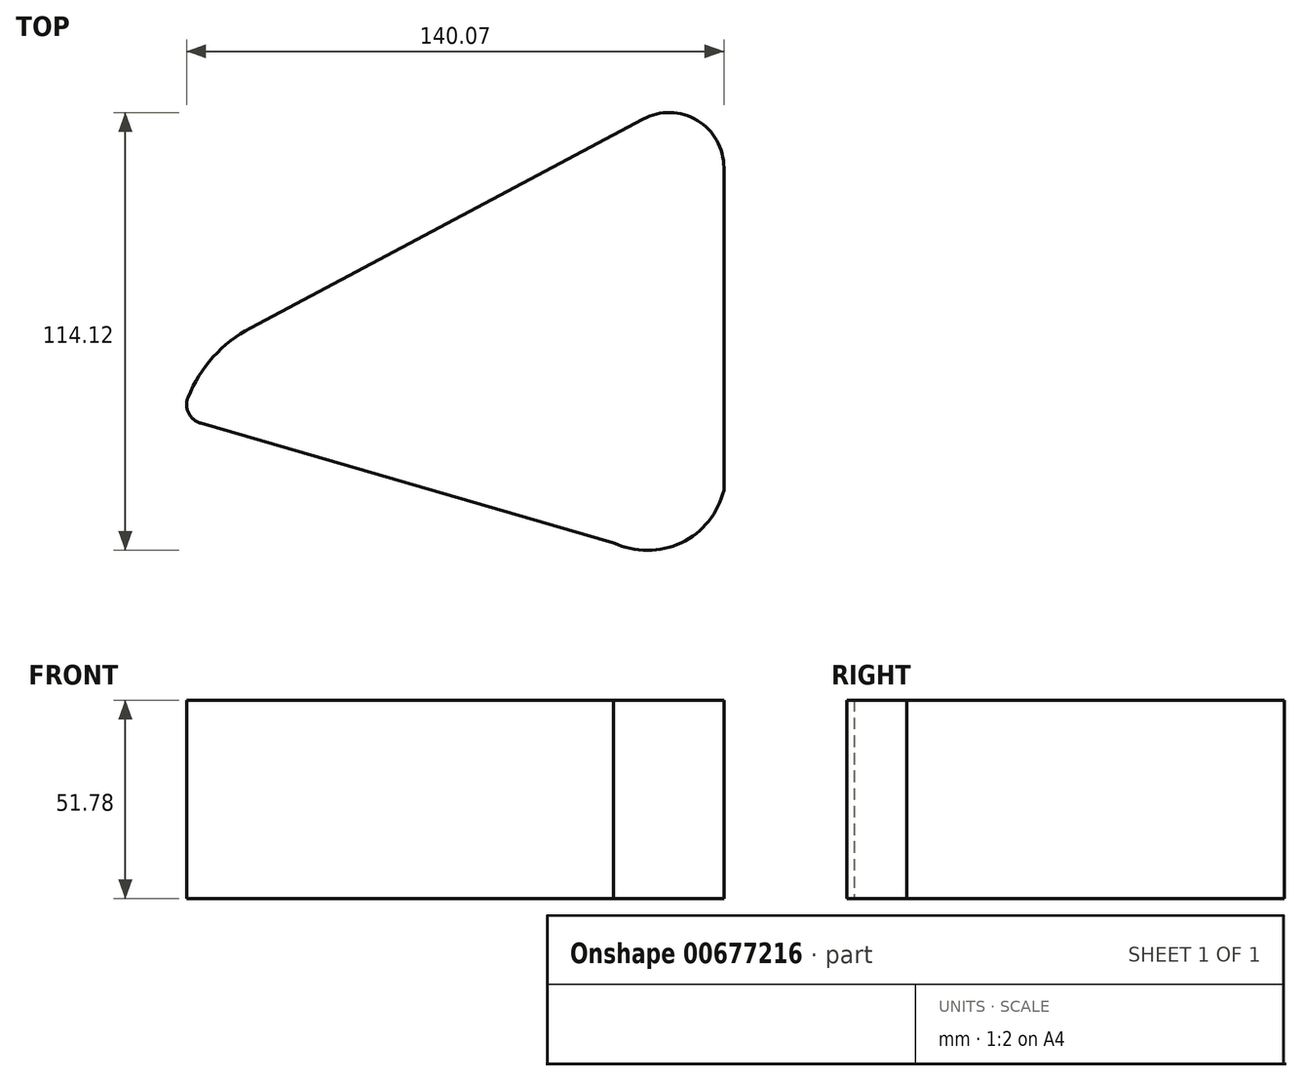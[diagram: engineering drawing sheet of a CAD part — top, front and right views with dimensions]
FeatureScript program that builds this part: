
annotation { "Feature Type Name" : "Feature", "Feature Type Description" : "" }
export const myFeature = defineFeature(function(context is Context, id is Id, definition is map)
    precondition{}
    {
        {
            var Q0;
            Q0=qCreatedBy(makeId("Top.planeOp"),FACE);
            var sketch = newSketch(context, id + "F0", { "sketchPlane" : qUnion([Q0])});
            skLineSegment(sketch, "E0", {"start": v(-75.31, -14.42) * mm, "end": v(37.3, -47.02) * mm});
            skLineSegment(sketch, "E1", {"start": v(37.3, -47.02) * mm, "end": v(37.3, -47.02) * mm});
            skArc(sketch, "E2", {"start": v(37.3, -47.02) * mm, "mid": v(54.96, -47.02) * mm, "end": v(66.07, -33.3) * mm});
            skLineSegment(sketch, "E3", {"start": v(66.07, -33.3) * mm, "end": v(66.07, 50.8) * mm});
            skArc(sketch, "E4", {"start": v(66.07, 50.8) * mm, "mid": v(59.12, 63.06) * mm, "end": v(45.03, 63.43) * mm});
            skLineSegment(sketch, "E5", {"start": v(45.03, 63.43) * mm, "end": v(-57.35, 8.99) * mm});
            skArc(sketch, "E6", {"start": v(-57.35, 8.99) * mm, "mid": v(-68.87, -0.77) * mm, "end": v(-75.31, -14.42) * mm});
            skSolve(sketch);
        }
        {
            var Q0;
            Q0=makeQuery(id+"F0.imprint","IMPRINT",FACE,{"disambiguationData":[TD([[makeQuery(id+"F0.imprint","IMPRINT",EDGE,{"derivedFrom":sQuery(id+"F0.wireOp",EDGE,"E0")}),1.0]])]});
            extrude(context, id + "F1", {"entities" : qUnion([Q0]), "depth" : 51.78 * mm, "offsetDistance" : 25.4 * mm});
        }
        {
            var Q0;
            Q0=makeQuery(id+"F1.opExtrude","SWEPT_EDGE",EDGE,{"disambiguationData":[OSD([sQuery(id+"F0.wireOp",EDGE,"E0"),sQuery(id+"F0.wireOp",EDGE,"E6")])]});
            fillet(context, id + "F2", {"entities" : qUnion([Q0]), "radius" : 5.08 * mm, "tangentPropagation" : true, "allowEdgeOverflow" : false});
        }
    });
